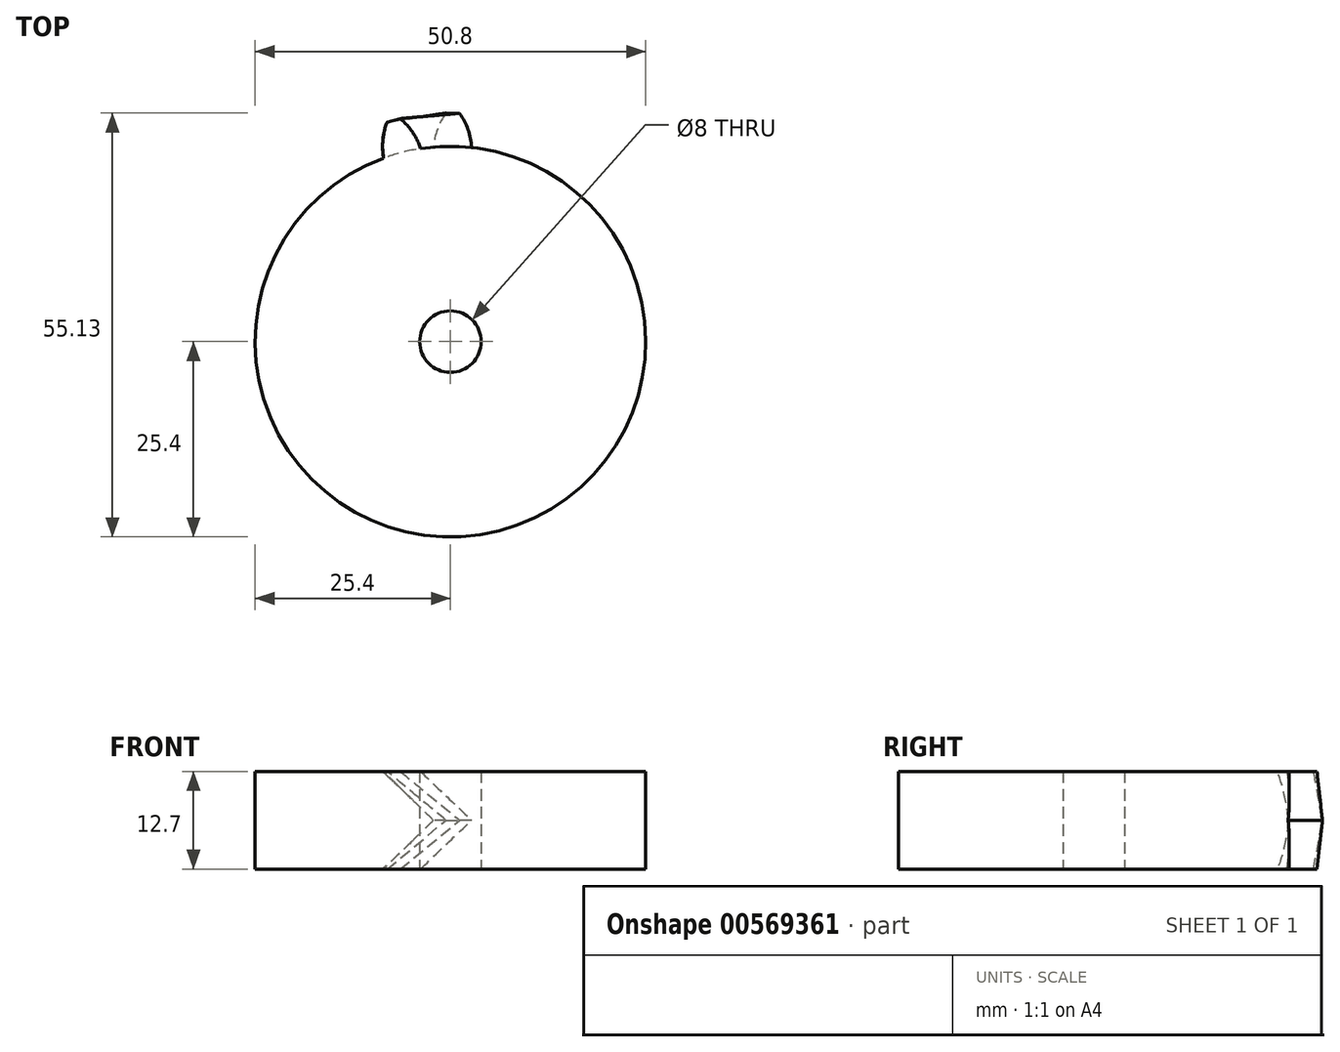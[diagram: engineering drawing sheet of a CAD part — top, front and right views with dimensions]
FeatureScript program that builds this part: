
annotation { "Feature Type Name" : "Feature", "Feature Type Description" : "" }
export const myFeature = defineFeature(function(context is Context, id is Id, definition is map)
    precondition{}
    {
        {
            var Q0;
            Q0=qCreatedBy(makeId("Top.planeOp"),FACE);
            var sketch = newSketch(context, id + "F0", { "sketchPlane" : qUnion([Q0])});
            skCircle(sketch, "E0", {"center": v(0, 0) * mm, "radius": 4 * mm});
            skCircle(sketch, "E1", {"center": v(0, 0) * mm, "radius": 25.4 * mm});
            skLineSegment(sketch, "E2", {"start": v(4.41, 25.01) * mm, "end": v(0, 0) * mm, "construction": true});
            skLineSegment(sketch, "E3", {"start": v(-4.41, 25.01) * mm, "end": v(0, 0) * mm, "construction": true});
            skLineSegment(sketch, "E4", {"start": v(-8.69, 23.87) * mm, "end": v(0, 0) * mm, "construction": true});
            skLineSegment(sketch, "E5", {"start": v(-7.64, 29.81) * mm, "end": v(29.71, 16.22) * mm, "construction": true});
            skLineSegment(sketch, "E6", {"start": v(8.69, 23.87) * mm, "end": v(29.88, 23.87) * mm, "construction": true});
            skLineSegment(sketch, "E7", {"start": v(-8.69, 23.87) * mm, "end": v(-20, 19.75) * mm, "construction": true});
            skLineSegment(sketch, "E8", {"start": v(-4.41, 25.01) * mm, "end": v(-10.92, 23.87) * mm, "construction": true});
            skLineSegment(sketch, "E9", {"start": v(4.41, 25.01) * mm, "end": v(-8.61, 27.31) * mm, "construction": true});
            skArc(sketch, "E10", {"start": v(-8.23, 28.57) * mm, "mid": v(-8.78, 26.25) * mm, "end": v(-8.69, 23.87) * mm});
            skLineSegment(sketch, "E11", {"start": v(0, 0) * mm, "end": v(0, 25.4) * mm, "construction": true});
            skLineSegment(sketch, "E12", {"start": v(0, 25.4) * mm, "end": v(-8.82, 25.4) * mm, "construction": true});
            skLineSegment(sketch, "E13", {"start": v(0, 0) * mm, "end": v(8.69, 23.87) * mm, "construction": true});
            skLineSegment(sketch, "E14", {"start": v(-7.64, 29.81) * mm, "end": v(0, 0) * mm, "construction": true});
            skArc(sketch, "E15.MirrorCS", {"start": v(-6.52, 29) * mm, "mid": v(-4.93, 27.24) * mm, "end": v(-3.86, 25.1) * mm});
            skLineSegment(sketch, "E16", {"start": v(-8.23, 28.57) * mm, "end": v(-6.52, 29) * mm});
            skPoint(sketch, "E17.orphan", {"position": v(-7.64, 29.81) * mm});
            skSolve(sketch);
        }
        {
            var Q0;
            Q0=qCreatedBy(makeId("Top.planeOp"),FACE);
            cPlane(context, id + "F1", {"entities" : qUnion([Q0]), "cplaneType" : CPlaneType.OFFSET, "offset" : 6.35 * mm, "width" : 152.4 * mm, "height" : 152.4 * mm});
        }
        {
            var Q0;
            Q0=qCreatedBy(id+"F1.planeOp",FACE);
            var sketch = newSketch(context, id + "F2", { "sketchPlane" : qUnion([Q0])});
            skCircle(sketch, "E18", {"center": v(0, 0) * mm, "radius": 4 * mm});
            skCircle(sketch, "E19", {"center": v(0, 0) * mm, "radius": 25.4 * mm});
            skLineSegment(sketch, "E20", {"start": v(10.73, 23.02) * mm, "end": v(0, 0) * mm, "construction": true});
            skLineSegment(sketch, "E21", {"start": v(2.21, 25.3) * mm, "end": v(0, 0) * mm, "construction": true});
            skLineSegment(sketch, "E22", {"start": v(-2.21, 25.3) * mm, "end": v(0, 0) * mm, "construction": true});
            skLineSegment(sketch, "E23", {"start": v(0.34, 30.77) * mm, "end": v(28.83, 10.82) * mm, "construction": true});
            skLineSegment(sketch, "E24", {"start": v(14.57, 20.8) * mm, "end": v(30.4, 16.57) * mm, "construction": true});
            skLineSegment(sketch, "E25", {"start": v(-2.21, 25.3) * mm, "end": v(-18.58, 23.87) * mm, "construction": true});
            skLineSegment(sketch, "E26", {"start": v(2.21, 25.3) * mm, "end": v(-8.83, 26.27) * mm, "construction": true});
            skLineSegment(sketch, "E27", {"start": v(10.73, 23.02) * mm, "end": v(-1.25, 28.6) * mm, "construction": true});
            skArc(sketch, "E28", {"start": v(-0.56, 29.73) * mm, "mid": v(-1.69, 27.63) * mm, "end": v(-2.21, 25.3) * mm});
            skLineSegment(sketch, "E29", {"start": v(0, 0) * mm, "end": v(6.57, 24.53) * mm, "construction": true});
            skLineSegment(sketch, "E30", {"start": v(6.57, 24.53) * mm, "end": v(-1.95, 26.82) * mm, "construction": true});
            skLineSegment(sketch, "E31", {"start": v(0, 0) * mm, "end": v(14.57, 20.8) * mm, "construction": true});
            skLineSegment(sketch, "E32", {"start": v(0.34, 30.77) * mm, "end": v(0, 0) * mm, "construction": true});
            skArc(sketch, "E33.MirrorCS", {"start": v(1.2, 29.7) * mm, "mid": v(2.3, 27.58) * mm, "end": v(2.77, 25.25) * mm});
            skLineSegment(sketch, "E34", {"start": v(-0.56, 29.73) * mm, "end": v(1.2, 29.7) * mm});
            skPoint(sketch, "E35.orphan", {"position": v(0.34, 30.77) * mm});
            skSolve(sketch);
        }
        {
            var Q0;
            Q0=makeQuery(id+"F0.imprint","IMPRINT",FACE,{"disambiguationData":[TD([[makeQuery(id+"F0.imprint","IMPRINT",EDGE,{"derivedFrom":sQuery(id+"F0.wireOp",EDGE,"E0")}),-1.0]])]});
            extrude(context, id + "F3", {"entities" : qUnion([Q0]), "depth" : 6.35 * mm, "offsetDistance" : 25.4 * mm});
        }
        {
            var Q1;
            {var subQ0=sQuery(id+"F0.wireOp",EDGE,"E10");Q1=makeQuery(id+"F0.imprint","IMPRINT",FACE,{"disambiguationData":[TD([[makeQuery(id+"F0.imprint","IMPRINT",EDGE,{"derivedFrom":subQ0}),1.0]])]});}
            var Q2;
            {var subQ0=sQuery(id+"F2.wireOp",EDGE,"E28");Q2=makeQuery(id+"F2.imprint","IMPRINT",FACE,{"disambiguationData":[TD([[makeQuery(id+"F2.imprint","IMPRINT",EDGE,{"derivedFrom":subQ0}),1.0]])]});}
            loft(context, id + "F4", {"operationType" : NewBodyOperationType.ADD, "sheetProfilesArray" : [{ "sheetProfileEntities" : qUnion([Q1]) }, { "sheetProfileEntities" : qUnion([Q2]) }]});
        }
        {
            var Q0;
            Q0=makeQuery(id+"F3.opExtrude","SWEPT_BODY",BODY,{"disambiguationData":[OSD([sQuery(id+"F0.wireOp",EDGE,"E0"),sQuery(id+"F0.wireOp",EDGE,"E1")])]});
            var Q1;
            {var subQ0=sQuery(id+"F2.wireOp",EDGE,"E28");Q1=makeQuery(id+"F4.boolean.opBoolean","MERGE",FACE,{"derivedFrom":[makeQuery(id+"F3.opExtrude","CAP_FACE",FACE,{"disambiguationData":[OSD([sQuery(id+"F0.wireOp",EDGE,"E0"),sQuery(id+"F0.wireOp",EDGE,"E1")])],"isStart":false}),makeQuery(id+"F4.opLoft","CAP_FACE",FACE,{"disambiguationData":[OSD([makeQuery(id+"F2.imprint","IMPRINT",FACE,{"disambiguationData":[TD([[makeQuery(id+"F2.imprint","IMPRINT",EDGE,{"derivedFrom":subQ0}),1.0]])]})])],"isStart":true})]});}
            mirror(context, id + "F5", {"operationType" : NewBodyOperationType.ADD, "entities" : qUnion([Q0]), "mirrorPlane" : qUnion([Q1])});
        }
    });
